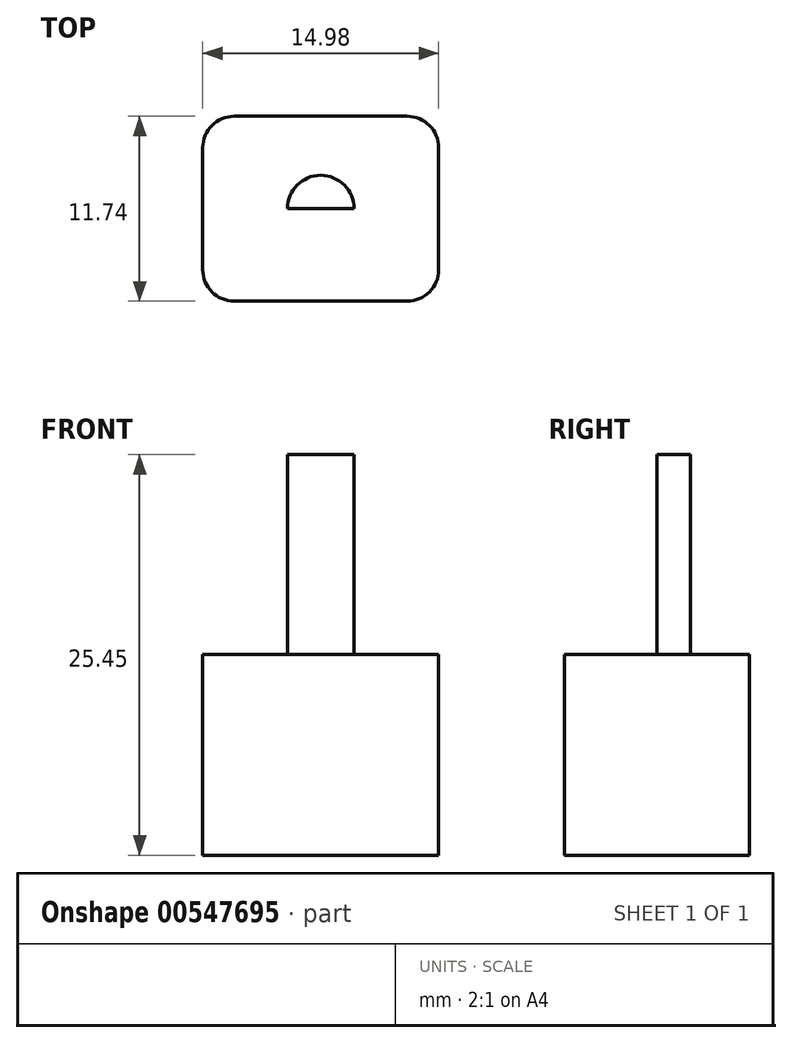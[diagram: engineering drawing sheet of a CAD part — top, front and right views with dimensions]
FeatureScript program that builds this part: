
annotation { "Feature Type Name" : "Feature", "Feature Type Description" : "" }
export const myFeature = defineFeature(function(context is Context, id is Id, definition is map)
    precondition{}
    {
        {
            var Q0;
            Q0=qCreatedBy(makeId("Top.planeOp"),FACE);
            var sketch = newSketch(context, id + "F0", { "sketchPlane" : qUnion([Q0])});
            skLineSegment(sketch, "E0.bottom", {"start": v(-5.5, 5.87) * mm, "end": v(5.5, 5.87) * mm});
            skLineSegment(sketch, "E0.top", {"start": v(-5.5, -5.87) * mm, "end": v(5.5, -5.87) * mm});
            skLineSegment(sketch, "E0.left", {"start": v(-7.5, 3.87) * mm, "end": v(-7.5, -3.87) * mm});
            skLineSegment(sketch, "E0.right", {"start": v(7.5, 3.87) * mm, "end": v(7.5, -3.87) * mm});
            skPoint(sketch, "E0.middle", {"position": v(0, 0) * mm});
            skPoint(sketch, "E1.visualSharp", {"position": v(7.5, 5.87) * mm});
            skArc(sketch, "E1.filletArc", {"start": v(7.5, 3.87) * mm, "mid": v(6.9, 5.29) * mm, "end": v(5.5, 5.87) * mm});
            skPoint(sketch, "E2.visualSharp", {"position": v(-7.5, 5.87) * mm});
            skArc(sketch, "E2.filletArc", {"start": v(-5.5, 5.87) * mm, "mid": v(-6.9, 5.29) * mm, "end": v(-7.5, 3.87) * mm});
            skPoint(sketch, "E3.visualSharp", {"position": v(-7.5, -5.87) * mm});
            skArc(sketch, "E3.filletArc", {"start": v(-7.5, -3.87) * mm, "mid": v(-6.9, -5.29) * mm, "end": v(-5.5, -5.87) * mm});
            skPoint(sketch, "E4.visualSharp", {"position": v(7.5, -5.87) * mm});
            skArc(sketch, "E4.filletArc", {"start": v(5.5, -5.87) * mm, "mid": v(6.9, -5.29) * mm, "end": v(7.5, -3.87) * mm});
            skSolve(sketch);
        }
        {
            var Q0;
            Q0 = qSketchRegion(id + "F0", true);
            extrude(context, id + "F1", {"entities" : qUnion([Q0]), "depth" : 12.75 * mm, "offsetDistance" : 25.4 * mm});
        }
        {
            var Q0;
            Q0=makeQuery(id+"F1.opExtrude","CAP_FACE",FACE,{"disambiguationData":[OSD([sQuery(id+"F0.wireOp",EDGE,"E0.bottom"),sQuery(id+"F0.wireOp",EDGE,"E0.top"),sQuery(id+"F0.wireOp",EDGE,"E0.left"),sQuery(id+"F0.wireOp",EDGE,"E0.right"),sQuery(id+"F0.wireOp",EDGE,"E1.filletArc"),sQuery(id+"F0.wireOp",EDGE,"E2.filletArc"),sQuery(id+"F0.wireOp",EDGE,"E3.filletArc"),sQuery(id+"F0.wireOp",EDGE,"E4.filletArc")])],"isStart":false});
            var sketch = newSketch(context, id + "F2", { "sketchPlane" : qUnion([Q0])});
            skCircle(sketch, "E5", {"center": v(0, 0) * mm, "radius": 2.12 * mm});
            skSolve(sketch);
        }
        {
            var Q0;
            Q0 = qSketchRegion(id + "F2", true);
            extrude(context, id + "F3", {"entities" : qUnion([Q0]), "operationType" : NewBodyOperationType.ADD, "depth" : 12.7 * mm, "offsetDistance" : 25.4 * mm});
        }
        {
            var Q0;
            Q0=makeQuery(id+"F3.opExtrude","CAP_FACE",FACE,{"disambiguationData":[OSD([sQuery(id+"F2.wireOp",EDGE,"E5")])],"isStart":false});
            var sketch = newSketch(context, id + "F4", { "sketchPlane" : qUnion([Q0])});
            skLineSegment(sketch, "E6", {"start": v(0, 0) * mm, "end": v(-2.12, 0) * mm});
            skLineSegment(sketch, "E7", {"start": v(0, 0) * mm, "end": v(2.12, 0) * mm});
            skSolve(sketch);
        }
        {
            var Q0;
            {var subQ0=sQuery(id+"F4.wireOp",EDGE,"E6");Q0=makeQuery(id+"F4.imprint","IMPRINT",FACE,{"disambiguationData":[TD([[makeQuery(id+"F4.imprint","IMPRINT",EDGE,{"derivedFrom":subQ0}),1.0]])]});}
            extrude(context, id + "F5", {"entities" : qUnion([Q0]), "operationType" : NewBodyOperationType.REMOVE, "oppositeDirection" : true, "depth" : 12.7 * mm, "offsetDistance" : 25.4 * mm});
        }
    });
